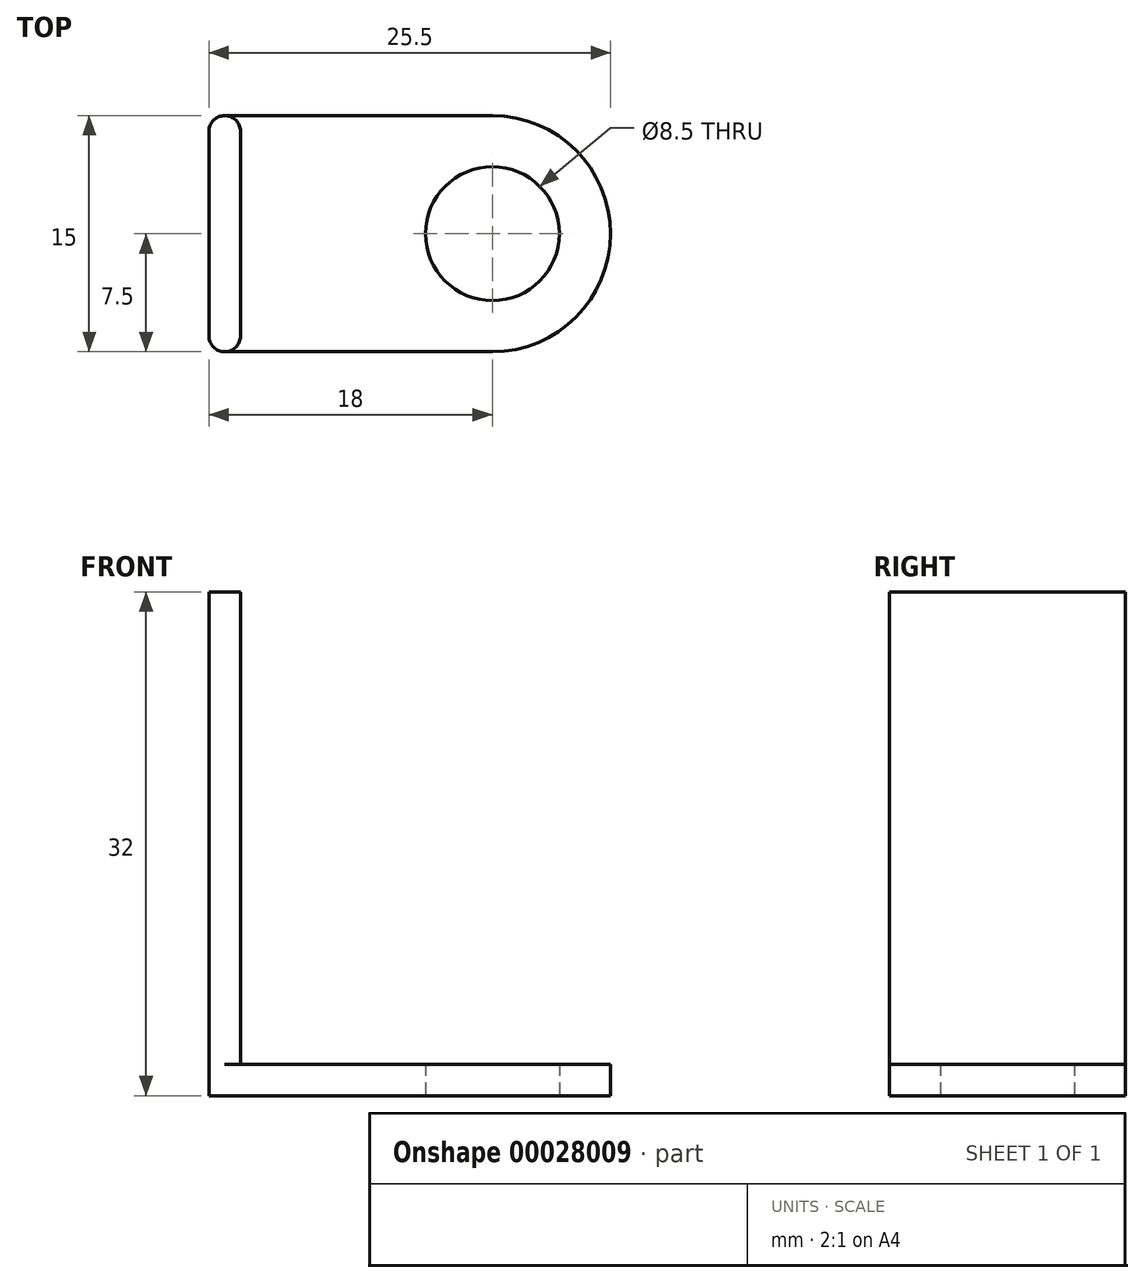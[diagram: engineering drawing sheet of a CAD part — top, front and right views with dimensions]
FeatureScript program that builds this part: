
annotation { "Feature Type Name" : "Feature", "Feature Type Description" : "" }
export const myFeature = defineFeature(function(context is Context, id is Id, definition is map)
    precondition{}
    {
        {
            var Q0;
            Q0=qCreatedBy(makeId("Top.planeOp"),FACE);
            var sketch = newSketch(context, id + "F0", { "sketchPlane" : qUnion([Q0])});
            skCircle(sketch, "E0", {"center": v(0, 0) * mm, "radius": 4.25 * mm});
            skArc(sketch, "E1", {"start": v(0, -7.5) * mm, "mid": v(7.5, 0) * mm, "end": v(0, 7.5) * mm});
            skLineSegment(sketch, "E2", {"start": v(0, -7.5) * mm, "end": v(-18, -7.5) * mm});
            skLineSegment(sketch, "E3", {"start": v(-18, -7.5) * mm, "end": v(-18, 7.5) * mm});
            skLineSegment(sketch, "E4", {"start": v(-18, 7.5) * mm, "end": v(0, 7.5) * mm});
            skSolve(sketch);
        }
        {
            var Q0;
            Q0=makeQuery(id+"F0.imprint","IMPRINT",FACE,{"disambiguationData":[TD([[makeQuery(id+"F0.imprint","IMPRINT",EDGE,{"derivedFrom":sQuery(id+"F0.wireOp",EDGE,"E0")}),-1.0]])]});
            extrude(context, id + "F1", {"entities" : qUnion([Q0]), "depth" : 2 * mm});
        }
        {
            var Q0;
            Q0=makeQuery(id+"F1.opExtrude","CAP_FACE",FACE,{"disambiguationData":[OSD([sQuery(id+"F0.wireOp",EDGE,"E0"),sQuery(id+"F0.wireOp",EDGE,"E1"),sQuery(id+"F0.wireOp",EDGE,"E2"),sQuery(id+"F0.wireOp",EDGE,"E3"),sQuery(id+"F0.wireOp",EDGE,"E4")])],"isStart":false});
            var sketch = newSketch(context, id + "F2", { "sketchPlane" : qUnion([Q0])});
            skLineSegment(sketch, "E5.bottom", {"start": v(-18, 7.5) * mm, "end": v(-16, 7.5) * mm});
            skLineSegment(sketch, "E5.top", {"start": v(-18, -7.5) * mm, "end": v(-16, -7.5) * mm});
            skLineSegment(sketch, "E5.left", {"start": v(-18, 7.5) * mm, "end": v(-18, -7.5) * mm});
            skLineSegment(sketch, "E5.right", {"start": v(-16, 7.5) * mm, "end": v(-16, -7.5) * mm});
            skSolve(sketch);
        }
        {
            var Q0;
            Q0=makeQuery(id+"F2.imprint","IMPRINT",FACE,{"disambiguationData":[TD([[makeQuery(id+"F2.imprint","IMPRINT",EDGE,{"derivedFrom":sQuery(id+"F2.wireOp",EDGE,"E5.bottom")}),-1.0]])]});
            extrude(context, id + "F3", {"entities" : qUnion([Q0]), "operationType" : NewBodyOperationType.ADD, "depth" : 30 * mm});
        }
        {
            var Q0;
            Q0=makeQuery(id+"F3.boolean.opBoolean","MERGE",EDGE,{"derivedFrom":[makeQuery(id+"F1.opExtrude","SWEPT_EDGE",EDGE,{"disambiguationData":[OSD([sQuery(id+"F0.wireOp",EDGE,"E2"),sQuery(id+"F0.wireOp",EDGE,"E3")])]}),makeQuery(id+"F3.opExtrude","SWEPT_EDGE",EDGE,{"disambiguationData":[OSD([sQuery(id+"F2.wireOp",EDGE,"E5.top"),sQuery(id+"F2.wireOp",EDGE,"E5.left")])]})]});
            var Q1;
            Q1=makeQuery(id+"F3.opExtrude","SWEPT_EDGE",EDGE,{"disambiguationData":[OSD([sQuery(id+"F0.wireOp",EDGE,"E2"),sQuery(id+"F2.wireOp",EDGE,"E5.top"),sQuery(id+"F2.wireOp",EDGE,"E5.right")])]});
            var Q2;
            Q2=makeQuery(id+"F3.boolean.opBoolean","MERGE",EDGE,{"derivedFrom":[makeQuery(id+"F1.opExtrude","SWEPT_EDGE",EDGE,{"disambiguationData":[OSD([sQuery(id+"F0.wireOp",EDGE,"E3"),sQuery(id+"F0.wireOp",EDGE,"E4")])]}),makeQuery(id+"F3.opExtrude","SWEPT_EDGE",EDGE,{"disambiguationData":[OSD([sQuery(id+"F2.wireOp",EDGE,"E5.bottom"),sQuery(id+"F2.wireOp",EDGE,"E5.left")])]})]});
            var Q3;
            Q3=makeQuery(id+"F3.opExtrude","SWEPT_EDGE",EDGE,{"disambiguationData":[OSD([sQuery(id+"F0.wireOp",EDGE,"E4"),sQuery(id+"F2.wireOp",EDGE,"E5.bottom"),sQuery(id+"F2.wireOp",EDGE,"E5.right")])]});
            fillet(context, id + "F4", {"entities" : qUnion([Q0, Q1, Q2, Q3]), "radius" : 1 * mm, "allowEdgeOverflow" : false});
        }
    });
